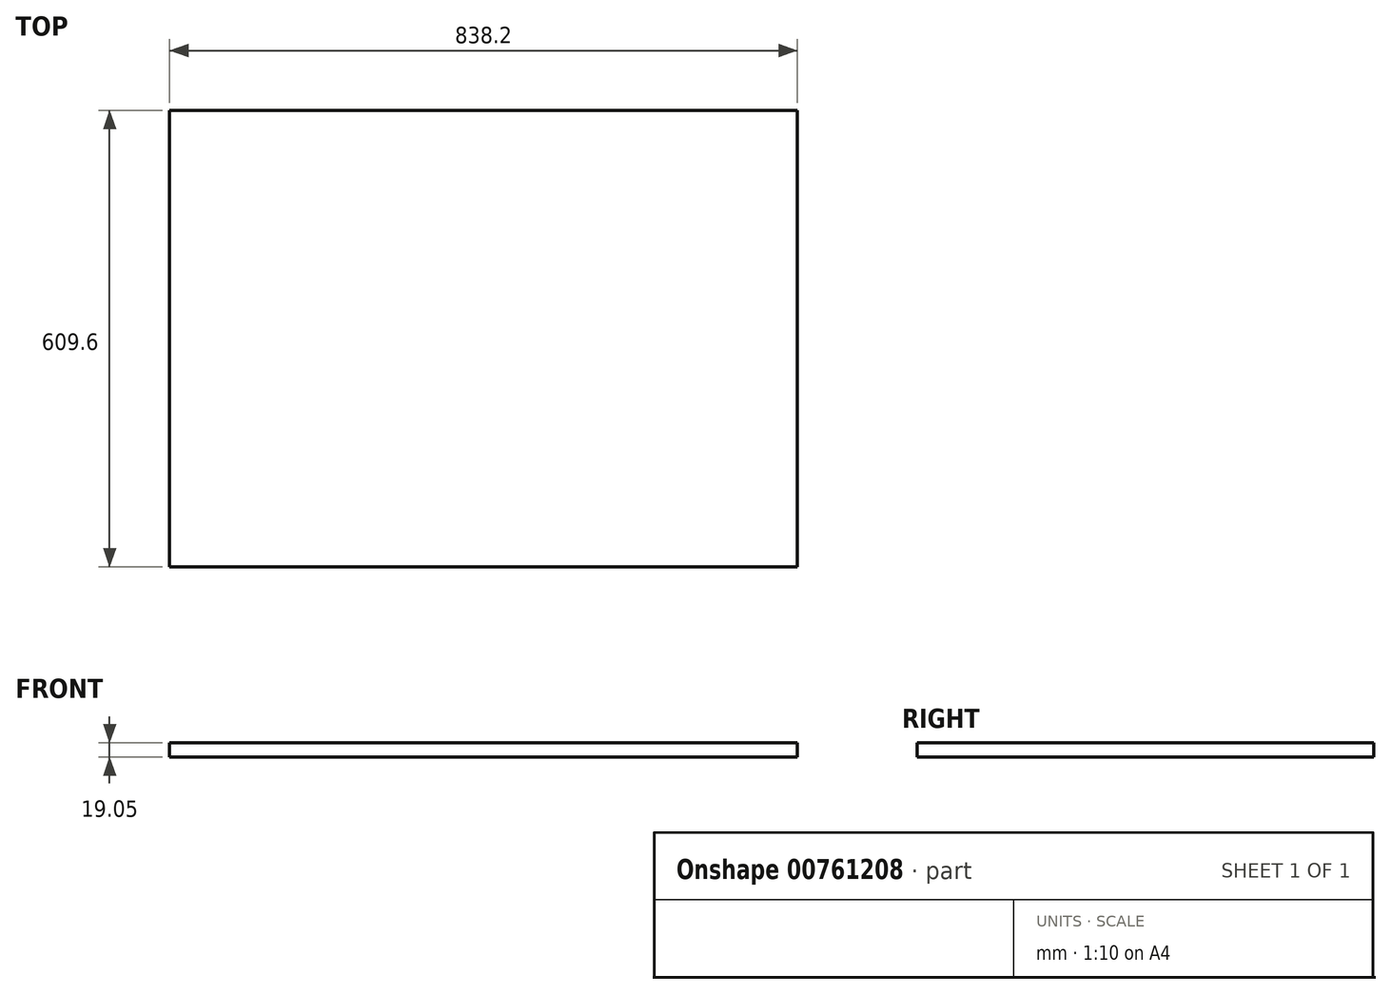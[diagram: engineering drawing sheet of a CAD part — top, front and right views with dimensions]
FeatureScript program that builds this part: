
annotation { "Feature Type Name" : "Feature", "Feature Type Description" : "" }
export const myFeature = defineFeature(function(context is Context, id is Id, definition is map)
    precondition{}
    {
        {
            var Q0;
            Q0=qCreatedBy(makeId("Top.planeOp"),FACE);
            var sketch = newSketch(context, id + "F0", { "sketchPlane" : qUnion([Q0])});
            skLineSegment(sketch, "E0.bottom", {"start": v(-435.28, -369.63) * mm, "end": v(402.92, -369.63) * mm});
            skLineSegment(sketch, "E0.top", {"start": v(-435.28, 239.97) * mm, "end": v(402.92, 239.97) * mm});
            skLineSegment(sketch, "E0.left", {"start": v(-435.28, -369.63) * mm, "end": v(-435.28, 239.97) * mm});
            skLineSegment(sketch, "E0.right", {"start": v(402.92, -369.63) * mm, "end": v(402.92, 239.97) * mm});
            skSolve(sketch);
        }
        {
            var Q0;
            Q0=makeQuery(id+"F0.imprint","IMPRINT",FACE,{"disambiguationData":[TD([[makeQuery(id+"F0.imprint","IMPRINT",EDGE,{"derivedFrom":sQuery(id+"F0.wireOp",EDGE,"E0.bottom")}),1.0]])]});
            extrude(context, id + "F1", {"entities" : qUnion([Q0]), "depth" : 19.05 * mm, "offsetDistance" : 25.4 * mm});
        }
    });
